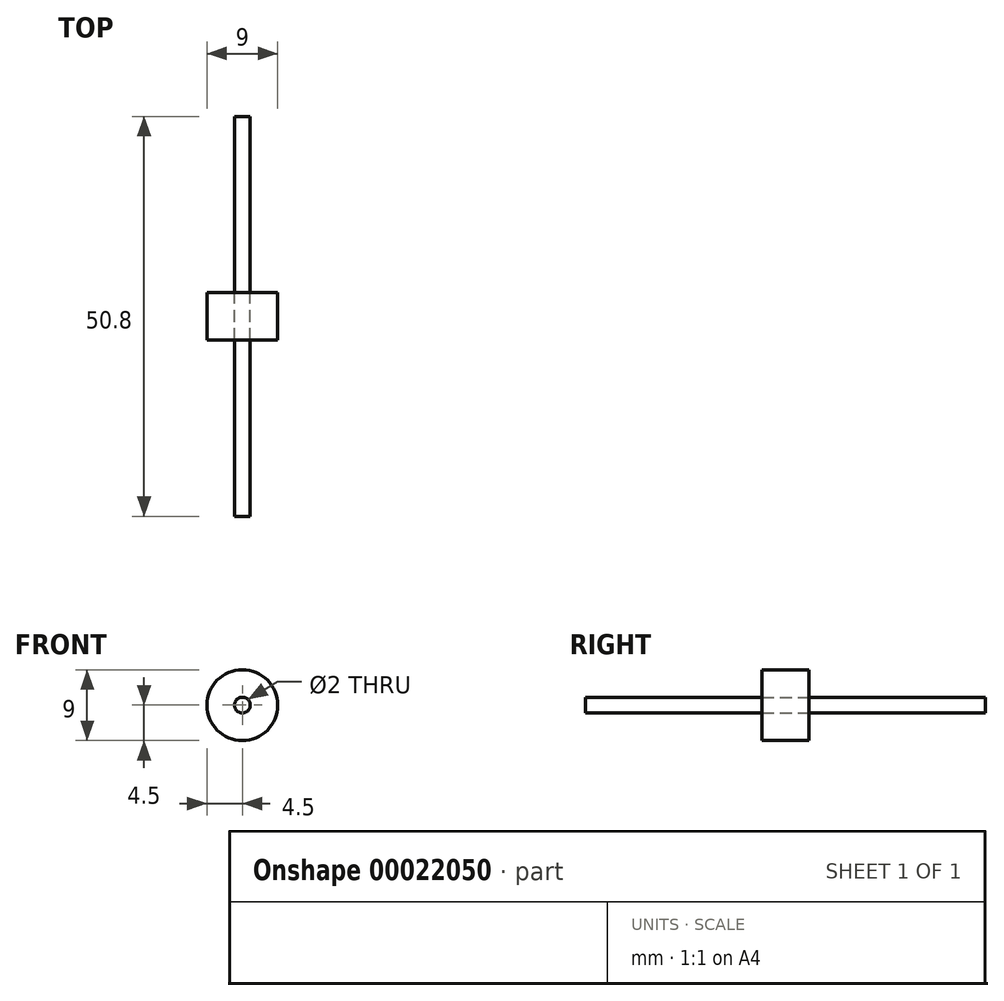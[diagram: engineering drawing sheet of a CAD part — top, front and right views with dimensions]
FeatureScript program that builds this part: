
annotation { "Feature Type Name" : "Feature", "Feature Type Description" : "" }
export const myFeature = defineFeature(function(context is Context, id is Id, definition is map)
    precondition{}
    {
        {
            var Q0;
            Q0=qCreatedBy(makeId("Front.planeOp"),FACE);
            var sketch = newSketch(context, id + "F0", { "sketchPlane" : qUnion([Q0])});
            skCircle(sketch, "E0", {"center": v(0, 0) * mm, "radius": 1 * mm});
            skCircle(sketch, "E1", {"center": v(0, 0) * mm, "radius": 4.5 * mm});
            skSolve(sketch);
        }
        {
            var Q0;
            Q0=makeQuery(id+"F0.imprint","IMPRINT",FACE,{"disambiguationData":[TD([[makeQuery(id+"F0.imprint","IMPRINT",EDGE,{"derivedFrom":sQuery(id+"F0.wireOp",EDGE,"E0")}),-1.0]])]});
            extrude(context, id + "F1", {"entities" : qUnion([Q0]), "endBound" : BoundingType.SYMMETRIC, "depth" : 6 * mm});
        }
        {
            var Q0;
            Q0=makeQuery(id+"F0.imprint","IMPRINT",FACE,{"disambiguationData":[TD([[makeQuery(id+"F0.imprint","IMPRINT",EDGE,{"derivedFrom":sQuery(id+"F0.wireOp",EDGE,"E0")}),1.0]])]});
            extrude(context, id + "F2", {"entities" : qUnion([Q0]), "endBound" : BoundingType.SYMMETRIC, "depth" : 50.8 * mm});
        }
    });
